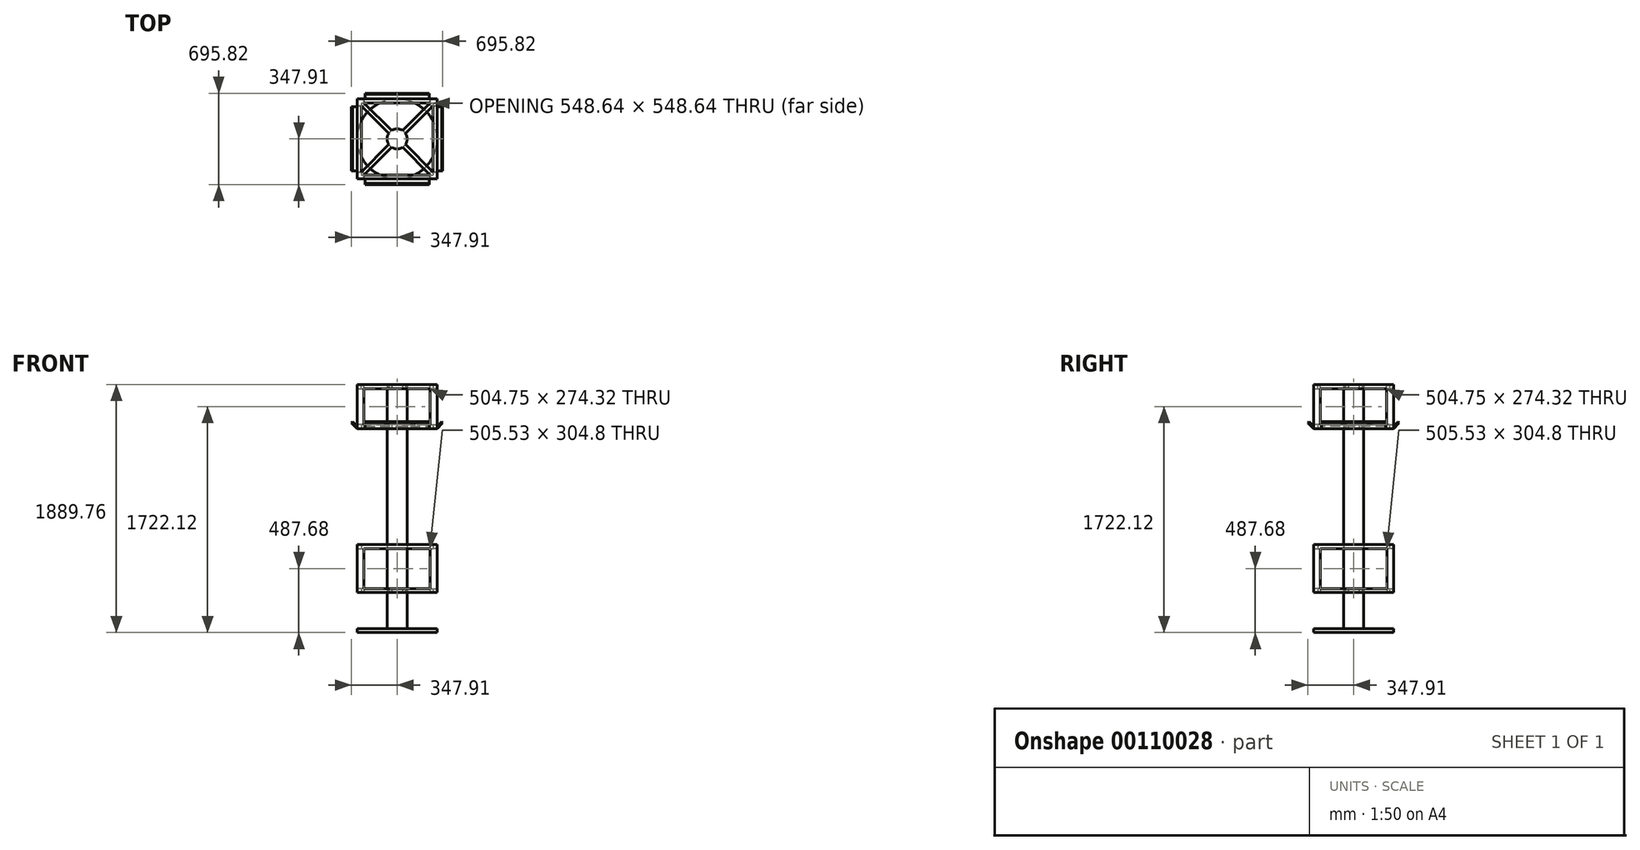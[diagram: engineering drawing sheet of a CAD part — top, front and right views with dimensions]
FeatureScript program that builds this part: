
annotation { "Feature Type Name" : "Feature", "Feature Type Description" : "" }
export const myFeature = defineFeature(function(context is Context, id is Id, definition is map)
    precondition{}
    {
        {
            var Q0;
            Q0=qCreatedBy(makeId("Top.planeOp"),FACE);
            var sketch = newSketch(context, id + "F0", { "sketchPlane" : qUnion([Q0])});
            skCircle(sketch, "E0", {"center": v(0, 0) * mm, "radius": 304.8 * mm});
            skSolve(sketch);
        }
        {
            var Q0;
            Q0 = qSketchRegion(id + "F0", true);
            extrude(context, id + "F1", {"entities" : qUnion([Q0]), "depth" : 30.48 * mm});
        }
        {
            var Q0;
            Q0=makeQuery(id+"F1.opExtrude","CAP_FACE",FACE,{"disambiguationData":[OSD([sQuery(id+"F0.wireOp",EDGE,"E0")])],"isStart":false});
            var sketch = newSketch(context, id + "F2", { "sketchPlane" : qUnion([Q0])});
            skCircle(sketch, "E1", {"center": v(0, 0) * mm, "radius": 76.2 * mm});
            skSolve(sketch);
        }
        {
            var Q0;
            Q0 = qSketchRegion(id + "F2", true);
            extrude(context, id + "F3", {"entities" : qUnion([Q0]), "operationType" : NewBodyOperationType.ADD, "depth" : 274.32 * mm});
        }
        {
            var Q0;
            Q0=makeQuery(id+"F3.opExtrude","CAP_FACE",FACE,{"disambiguationData":[OSD([sQuery(id+"F2.wireOp",EDGE,"E1")])],"isStart":false});
            var sketch = newSketch(context, id + "F4", { "sketchPlane" : qUnion([Q0])});
            skLineSegment(sketch, "E2.bottom", {"start": v(304.8, -304.8) * mm, "end": v(-304.8, -304.8) * mm});
            skLineSegment(sketch, "E2.top", {"start": v(304.8, 304.8) * mm, "end": v(-304.8, 304.8) * mm});
            skLineSegment(sketch, "E2.left", {"start": v(304.8, -304.8) * mm, "end": v(304.8, 304.8) * mm});
            skLineSegment(sketch, "E2.right", {"start": v(-304.8, -304.8) * mm, "end": v(-304.8, 304.8) * mm});
            skPoint(sketch, "E2.middle", {"position": v(0, 0) * mm});
            skLineSegment(sketch, "E3.bottom", {"start": v(252.77, -274.32) * mm, "end": v(-252.77, -274.32) * mm});
            skLineSegment(sketch, "E3.top", {"start": v(252.77, 274.32) * mm, "end": v(-252.77, 274.32) * mm});
            skLineSegment(sketch, "E3.left", {"start": v(274.32, -252.77) * mm, "end": v(274.32, 252.77) * mm});
            skLineSegment(sketch, "E3.right", {"start": v(-274.32, -252.77) * mm, "end": v(-274.32, 252.77) * mm});
            skLineSegment(sketch, "E4", {"start": v(-274.32, 274.32) * mm, "end": v(0, 0) * mm, "construction": true});
            skLineSegment(sketch, "E5", {"start": v(0, 0) * mm, "end": v(274.32, -274.32) * mm, "construction": true});
            skLineSegment(sketch, "E6", {"start": v(0, 0) * mm, "end": v(274.32, 274.32) * mm, "construction": true});
            skLineSegment(sketch, "E7", {"start": v(0, 0) * mm, "end": v(-274.32, -274.32) * mm, "construction": true});
            skLineSegment(sketch, "E8", {"start": v(0, 0) * mm, "end": v(-10.78, 10.78) * mm, "construction": true});
            skLineSegment(sketch, "E9", {"start": v(-10.78, 10.78) * mm, "end": v(0, 0) * mm, "construction": true});
            skLineSegment(sketch, "E10", {"start": v(0, 0) * mm, "end": v(10.78, 10.78) * mm, "construction": true});
            skLineSegment(sketch, "E11", {"start": v(10.78, 10.78) * mm, "end": v(0, 0) * mm, "construction": true});
            skLineSegment(sketch, "E12", {"start": v(0, 0) * mm, "end": v(53.88, -53.88) * mm, "construction": true});
            skLineSegment(sketch, "E13", {"start": v(0, 0) * mm, "end": v(-10.78, -10.78) * mm, "construction": true});
            skLineSegment(sketch, "E14", {"start": v(-10.78, -10.78) * mm, "end": v(0, 0) * mm, "construction": true});
            skLineSegment(sketch, "E15", {"start": v(0, 0) * mm, "end": v(10.78, -10.78) * mm, "construction": true});
            skLineSegment(sketch, "E16", {"start": v(10.78, -10.78) * mm, "end": v(0, 0) * mm, "construction": true});
            skLineSegment(sketch, "E17", {"start": v(-21.55, 0) * mm, "end": v(-274.32, -252.77) * mm});
            skLineSegment(sketch, "E18", {"start": v(0, -21.55) * mm, "end": v(-252.77, -274.32) * mm});
            skLineSegment(sketch, "E19", {"start": v(21.55, 0) * mm, "end": v(274.32, 252.77) * mm});
            skLineSegment(sketch, "E20", {"start": v(0, 21.55) * mm, "end": v(252.77, 274.32) * mm});
            skLineSegment(sketch, "E21", {"start": v(21.55, 0) * mm, "end": v(274.32, -252.77) * mm});
            skLineSegment(sketch, "E22", {"start": v(0, -21.55) * mm, "end": v(252.77, -274.32) * mm});
            skLineSegment(sketch, "E23", {"start": v(0, 21.55) * mm, "end": v(-252.77, 274.32) * mm});
            skLineSegment(sketch, "E24", {"start": v(-21.55, 0) * mm, "end": v(-274.32, 252.77) * mm});
            skSolve(sketch);
        }
        {
            var Q0;
            Q0 = qSketchRegion(id + "F4", true);
            extrude(context, id + "F5", {"entities" : qUnion([Q0]), "operationType" : NewBodyOperationType.ADD, "depth" : 30.48 * mm});
        }
        {
            var Q0;
            Q0=makeQuery(id+"F5.opExtrude","CAP_FACE",FACE,{"disambiguationData":[OSD([sQuery(id+"F4.wireOp",EDGE,"E2.bottom"),sQuery(id+"F4.wireOp",EDGE,"E2.top"),sQuery(id+"F4.wireOp",EDGE,"E2.left"),sQuery(id+"F4.wireOp",EDGE,"E2.right"),sQuery(id+"F4.wireOp",EDGE,"E3.bottom"),sQuery(id+"F4.wireOp",EDGE,"E3.top"),sQuery(id+"F4.wireOp",EDGE,"E3.left"),sQuery(id+"F4.wireOp",EDGE,"E3.right"),sQuery(id+"F4.wireOp",EDGE,"E17"),sQuery(id+"F4.wireOp",EDGE,"E18"),sQuery(id+"F4.wireOp",EDGE,"E19"),sQuery(id+"F4.wireOp",EDGE,"E20"),sQuery(id+"F4.wireOp",EDGE,"E21"),sQuery(id+"F4.wireOp",EDGE,"E22"),sQuery(id+"F4.wireOp",EDGE,"E23"),sQuery(id+"F4.wireOp",EDGE,"E24")])],"isStart":false});
            var sketch = newSketch(context, id + "F6", { "sketchPlane" : qUnion([Q0])});
            skCircle(sketch, "E25", {"center": v(0, 0) * mm, "radius": 76.2 * mm});
            skLineSegment(sketch, "E26.bottom", {"start": v(-304.8, 304.8) * mm, "end": v(-252.77, 304.8) * mm});
            skLineSegment(sketch, "E26.top", {"start": v(-304.8, 252.77) * mm, "end": v(-252.77, 252.77) * mm});
            skLineSegment(sketch, "E26.left", {"start": v(-304.8, 304.8) * mm, "end": v(-304.8, 252.77) * mm});
            skLineSegment(sketch, "E26.right", {"start": v(-252.77, 304.8) * mm, "end": v(-252.77, 252.77) * mm});
            skLineSegment(sketch, "E27.bottom", {"start": v(304.8, 304.8) * mm, "end": v(252.77, 304.8) * mm});
            skLineSegment(sketch, "E27.top", {"start": v(304.8, 252.77) * mm, "end": v(252.77, 252.77) * mm});
            skLineSegment(sketch, "E27.left", {"start": v(304.8, 304.8) * mm, "end": v(304.8, 252.77) * mm});
            skLineSegment(sketch, "E27.right", {"start": v(252.77, 304.8) * mm, "end": v(252.77, 252.77) * mm});
            skLineSegment(sketch, "E28.bottom", {"start": v(304.8, -304.8) * mm, "end": v(252.77, -304.8) * mm});
            skLineSegment(sketch, "E28.top", {"start": v(304.8, -252.77) * mm, "end": v(252.77, -252.77) * mm});
            skLineSegment(sketch, "E28.left", {"start": v(304.8, -304.8) * mm, "end": v(304.8, -252.77) * mm});
            skLineSegment(sketch, "E28.right", {"start": v(252.77, -304.8) * mm, "end": v(252.77, -252.77) * mm});
            skLineSegment(sketch, "E29.bottom", {"start": v(-304.8, -304.8) * mm, "end": v(-252.77, -304.8) * mm});
            skLineSegment(sketch, "E29.top", {"start": v(-304.8, -252.77) * mm, "end": v(-252.77, -252.77) * mm});
            skLineSegment(sketch, "E29.left", {"start": v(-304.8, -304.8) * mm, "end": v(-304.8, -252.77) * mm});
            skLineSegment(sketch, "E29.right", {"start": v(-252.77, -304.8) * mm, "end": v(-252.77, -252.77) * mm});
            skSolve(sketch);
        }
        {
            var Q0;
            Q0 = qSketchRegion(id + "F6", true);
            extrude(context, id + "F7", {"entities" : qUnion([Q0]), "operationType" : NewBodyOperationType.ADD, "depth" : 304.8 * mm, "hasSecondDirection" : true, "secondDirectionOppositeDirection" : true, "secondDirectionDepth" : 30.48 * mm});
        }
        {
            var Q0;
            Q0=makeQuery(id+"F7.opExtrude","CAP_FACE",FACE,{"disambiguationData":[OSD([sQuery(id+"F6.wireOp",EDGE,"E26.bottom"),sQuery(id+"F6.wireOp",EDGE,"E26.top"),sQuery(id+"F6.wireOp",EDGE,"E26.left"),sQuery(id+"F6.wireOp",EDGE,"E26.right")])],"isStart":false});
            var sketch = newSketch(context, id + "F8", { "sketchPlane" : qUnion([Q0])});
            skLineSegment(sketch, "E30.bottom", {"start": v(-304.8, 304.8) * mm, "end": v(304.8, 304.8) * mm});
            skLineSegment(sketch, "E30.top", {"start": v(-304.8, -304.8) * mm, "end": v(304.8, -304.8) * mm});
            skLineSegment(sketch, "E30.left", {"start": v(-304.8, 304.8) * mm, "end": v(-304.8, -304.8) * mm});
            skLineSegment(sketch, "E30.right", {"start": v(304.8, 304.8) * mm, "end": v(304.8, -304.8) * mm});
            skPoint(sketch, "E30.middle", {"position": v(0, 0) * mm});
            skLineSegment(sketch, "E31.bottom", {"start": v(-274.32, 274.32) * mm, "end": v(274.32, 274.32) * mm});
            skLineSegment(sketch, "E31.top", {"start": v(-274.32, -274.32) * mm, "end": v(274.32, -274.32) * mm});
            skLineSegment(sketch, "E31.left", {"start": v(-274.32, 274.32) * mm, "end": v(-274.32, -274.32) * mm});
            skLineSegment(sketch, "E31.right", {"start": v(274.32, 274.32) * mm, "end": v(274.32, -274.32) * mm});
            skSolve(sketch);
        }
        {
            var Q0;
            Q0 = qSketchRegion(id + "F8", true);
            var Q1;
            Q1=makeQuery(id+"F8.imprint","IMPRINT",FACE,{"disambiguationData":[TD([[makeQuery(id+"F8.imprint","IMPRINT",EDGE,{"derivedFrom":sQuery(id+"F8.wireOp",EDGE,"W6p5EcQz-eB1s-PhT1-Hnmv-3Ggb0HC7lHr9")}),1.0]])]});
            extrude(context, id + "F9", {"entities" : qUnion([Q0, Q1]), "operationType" : NewBodyOperationType.ADD, "depth" : 30.48 * mm});
        }
        {
            var Q0;
            Q0=makeQuery(id+"F7.opExtrude","CAP_FACE",FACE,{"disambiguationData":[OSD([sQuery(id+"F6.wireOp",EDGE,"E25")])],"isStart":false});
            var sketch = newSketch(context, id + "F10", { "sketchPlane" : qUnion([Q0])});
            skLineSegment(sketch, "E32.bottom", {"start": v(-304.8, 304.8) * mm, "end": v(304.8, 304.8) * mm});
            skLineSegment(sketch, "E32.top", {"start": v(-304.8, -304.8) * mm, "end": v(304.8, -304.8) * mm});
            skLineSegment(sketch, "E32.left", {"start": v(-304.8, 304.8) * mm, "end": v(-304.8, -304.8) * mm});
            skLineSegment(sketch, "E32.right", {"start": v(304.8, 304.8) * mm, "end": v(304.8, -304.8) * mm});
            skPoint(sketch, "E32.middle", {"position": v(0, 0) * mm});
            skLineSegment(sketch, "E33.bottom", {"start": v(-304.8, 304.8) * mm, "end": v(-252.37, 304.8) * mm});
            skLineSegment(sketch, "E33.top", {"start": v(-304.8, 252.37) * mm, "end": v(-252.37, 252.37) * mm});
            skLineSegment(sketch, "E33.left", {"start": v(-304.8, 304.8) * mm, "end": v(-304.8, 252.37) * mm});
            skLineSegment(sketch, "E33.right", {"start": v(-252.37, 304.8) * mm, "end": v(-252.37, 252.37) * mm});
            skLineSegment(sketch, "E34.bottom", {"start": v(-304.8, -304.8) * mm, "end": v(-252.37, -304.8) * mm});
            skLineSegment(sketch, "E34.top", {"start": v(-304.8, -252.37) * mm, "end": v(-252.37, -252.37) * mm});
            skLineSegment(sketch, "E34.left", {"start": v(-304.8, -304.8) * mm, "end": v(-304.8, -252.37) * mm});
            skLineSegment(sketch, "E34.right", {"start": v(-252.37, -304.8) * mm, "end": v(-252.37, -252.37) * mm});
            skLineSegment(sketch, "E35.bottom", {"start": v(304.8, 304.8) * mm, "end": v(252.37, 304.8) * mm});
            skLineSegment(sketch, "E35.top", {"start": v(304.8, 252.37) * mm, "end": v(252.37, 252.37) * mm});
            skLineSegment(sketch, "E35.left", {"start": v(304.8, 304.8) * mm, "end": v(304.8, 252.37) * mm});
            skLineSegment(sketch, "E35.right", {"start": v(252.37, 304.8) * mm, "end": v(252.37, 252.37) * mm});
            skLineSegment(sketch, "E36.bottom", {"start": v(304.8, -304.8) * mm, "end": v(252.37, -304.8) * mm});
            skLineSegment(sketch, "E36.top", {"start": v(304.8, -252.37) * mm, "end": v(252.37, -252.37) * mm});
            skLineSegment(sketch, "E36.left", {"start": v(304.8, -304.8) * mm, "end": v(304.8, -252.37) * mm});
            skLineSegment(sketch, "E36.right", {"start": v(252.37, -304.8) * mm, "end": v(252.37, -252.37) * mm});
            skCircle(sketch, "E37", {"center": v(0, 0) * mm, "radius": 76.2 * mm});
            skSolve(sketch);
        }
        {
            var Q0;
            Q0=makeQuery(id+"F10.imprint","IMPRINT",FACE,{"disambiguationData":[TD([[makeQuery(id+"F10.imprint","IMPRINT",EDGE,{"derivedFrom":sQuery(id+"F10.wireOp",EDGE,"E33.bottom")}),-1.0]])]});
            var Q1;
            Q1=makeQuery(id+"F10.imprint","IMPRINT",FACE,{"disambiguationData":[TD([[makeQuery(id+"F10.imprint","IMPRINT",EDGE,{"derivedFrom":sQuery(id+"F10.wireOp",EDGE,"E34.bottom")}),1.0]])]});
            var Q2;
            Q2=makeQuery(id+"F10.imprint","IMPRINT",FACE,{"disambiguationData":[TD([[makeQuery(id+"F10.imprint","IMPRINT",EDGE,{"derivedFrom":sQuery(id+"F10.wireOp",EDGE,"E35.bottom")}),1.0]])]});
            var Q3;
            Q3=makeQuery(id+"F10.imprint","IMPRINT",FACE,{"disambiguationData":[TD([[makeQuery(id+"F10.imprint","IMPRINT",EDGE,{"derivedFrom":sQuery(id+"F10.wireOp",EDGE,"E36.bottom")}),-1.0]])]});
            var Q4;
            Q4=makeQuery(id+"F10.imprint","IMPRINT",FACE,{"disambiguationData":[TD([[makeQuery(id+"F10.imprint","IMPRINT",EDGE,{"derivedFrom":sQuery(id+"F10.wireOp",EDGE,"E37")}),1.0]])]});
            extrude(context, id + "F11", {"entities" : qUnion([Q0, Q1, Q2, Q3, Q4]), "operationType" : NewBodyOperationType.ADD, "depth" : 914.4 * mm});
        }
        {
            var Q0;
            Q0=makeQuery(id+"F11.opExtrude","CAP_FACE",FACE,{"disambiguationData":[OSD([sQuery(id+"F10.wireOp",EDGE,"E37")])],"isStart":false});
            var sketch = newSketch(context, id + "F12", { "sketchPlane" : qUnion([Q0])});
            skLineSegment(sketch, "E38.bottom", {"start": v(304.8, -304.8) * mm, "end": v(-304.8, -304.8) * mm});
            skLineSegment(sketch, "E38.top", {"start": v(304.8, 304.8) * mm, "end": v(-304.8, 304.8) * mm});
            skLineSegment(sketch, "E38.left", {"start": v(304.8, -304.8) * mm, "end": v(304.8, 304.8) * mm});
            skLineSegment(sketch, "E38.right", {"start": v(-304.8, -304.8) * mm, "end": v(-304.8, 304.8) * mm});
            skPoint(sketch, "E38.middle", {"position": v(0, 0) * mm});
            skLineSegment(sketch, "E39.bottom", {"start": v(-252.37, 274.32) * mm, "end": v(252.37, 274.32) * mm});
            skLineSegment(sketch, "E39.top", {"start": v(-252.37, -274.32) * mm, "end": v(252.37, -274.32) * mm});
            skLineSegment(sketch, "E39.left", {"start": v(-274.32, 252.37) * mm, "end": v(-274.32, -252.37) * mm});
            skLineSegment(sketch, "E39.right", {"start": v(274.32, 252.37) * mm, "end": v(274.32, -252.37) * mm});
            skLineSegment(sketch, "E40.bottom", {"start": v(-304.8, 304.8) * mm, "end": v(-252.37, 304.8) * mm});
            skLineSegment(sketch, "E40.left", {"start": v(-304.8, 304.8) * mm, "end": v(-304.8, 252.37) * mm});
            skLineSegment(sketch, "E41.bottom", {"start": v(304.8, 304.8) * mm, "end": v(252.37, 304.8) * mm});
            skLineSegment(sketch, "E41.left", {"start": v(304.8, 304.8) * mm, "end": v(304.8, 252.37) * mm});
            skLineSegment(sketch, "E42.bottom", {"start": v(304.8, -304.8) * mm, "end": v(252.37, -304.8) * mm});
            skLineSegment(sketch, "E42.left", {"start": v(304.8, -304.8) * mm, "end": v(304.8, -252.37) * mm});
            skLineSegment(sketch, "E43.bottom", {"start": v(-304.8, -304.8) * mm, "end": v(-252.37, -304.8) * mm});
            skLineSegment(sketch, "E43.left", {"start": v(-304.8, -304.8) * mm, "end": v(-304.8, -252.37) * mm});
            skLineSegment(sketch, "E44", {"start": v(-274.32, 252.37) * mm, "end": v(-21.95, 0) * mm});
            skPoint(sketch, "E44.startSnap0", {"position": v(-278.59, 252.37) * mm});
            skLineSegment(sketch, "E45", {"start": v(-252.37, 274.32) * mm, "end": v(0, 21.95) * mm});
            skLineSegment(sketch, "E46", {"start": v(274.32, 252.37) * mm, "end": v(21.95, 0) * mm});
            skLineSegment(sketch, "E47", {"start": v(-274.32, -252.37) * mm, "end": v(-21.95, 0) * mm});
            skPoint(sketch, "E48.orphan", {"position": v(274.32, 274.32) * mm});
            skPoint(sketch, "E49.orphan", {"position": v(252.37, 252.37) * mm});
            skLineSegment(sketch, "E50.trimOffspring", {"start": v(21.95, 0) * mm, "end": v(274.32, -252.37) * mm});
            skLineSegment(sketch, "E51.trimOffspring", {"start": v(0, 21.95) * mm, "end": v(252.37, 274.32) * mm});
            skLineSegment(sketch, "E52.trimOffspring", {"start": v(0, -21.95) * mm, "end": v(252.37, -274.32) * mm});
            skLineSegment(sketch, "E53.trimOffspring", {"start": v(0, -21.95) * mm, "end": v(-252.37, -274.32) * mm});
            skPoint(sketch, "E54.orphan", {"position": v(-252.37, 252.37) * mm});
            skPoint(sketch, "E55.orphan", {"position": v(-274.32, 274.32) * mm});
            skPoint(sketch, "E56.orphan", {"position": v(-252.37, -252.37) * mm});
            skPoint(sketch, "E57.orphan", {"position": v(-274.32, -274.32) * mm});
            skPoint(sketch, "E58.orphan", {"position": v(274.32, -274.32) * mm});
            skPoint(sketch, "E42.right.end.orphan", {"position": v(252.37, -252.37) * mm});
            skSolve(sketch);
        }
        {
            var Q0;
            Q0 = qSketchRegion(id + "F12", true);
            extrude(context, id + "F13", {"entities" : qUnion([Q0]), "operationType" : NewBodyOperationType.ADD, "depth" : 30.48 * mm});
        }
        {
            var Q0;
            Q0=makeQuery(id+"F13.opExtrude","CAP_FACE",FACE,{"disambiguationData":[OSD([sQuery(id+"F12.wireOp",EDGE,"E38.bottom"),sQuery(id+"F12.wireOp",EDGE,"E38.top"),sQuery(id+"F12.wireOp",EDGE,"E38.left"),sQuery(id+"F12.wireOp",EDGE,"E38.right"),sQuery(id+"F12.wireOp",EDGE,"E39.bottom"),sQuery(id+"F12.wireOp",EDGE,"E39.top"),sQuery(id+"F12.wireOp",EDGE,"E39.left"),sQuery(id+"F12.wireOp",EDGE,"E39.right"),sQuery(id+"F12.wireOp",EDGE,"E40.bottom"),sQuery(id+"F12.wireOp",EDGE,"E40.left"),sQuery(id+"F12.wireOp",EDGE,"E41.bottom"),sQuery(id+"F12.wireOp",EDGE,"E41.left"),sQuery(id+"F12.wireOp",EDGE,"E42.bottom"),sQuery(id+"F12.wireOp",EDGE,"E42.left"),sQuery(id+"F12.wireOp",EDGE,"E43.bottom"),sQuery(id+"F12.wireOp",EDGE,"E43.left"),sQuery(id+"F12.wireOp",EDGE,"E44"),sQuery(id+"F12.wireOp",EDGE,"E45"),sQuery(id+"F12.wireOp",EDGE,"E46"),sQuery(id+"F12.wireOp",EDGE,"E47"),sQuery(id+"F12.wireOp",EDGE,"E50.trimOffspring"),sQuery(id+"F12.wireOp",EDGE,"E51.trimOffspring"),sQuery(id+"F12.wireOp",EDGE,"E52.trimOffspring"),sQuery(id+"F12.wireOp",EDGE,"E53.trimOffspring")])],"isStart":false});
            var sketch = newSketch(context, id + "F14", { "sketchPlane" : qUnion([Q0])});
            skLineSegment(sketch, "E59.bottom", {"start": v(-304.8, 304.8) * mm, "end": v(-252.37, 304.8) * mm});
            skLineSegment(sketch, "E59.top", {"start": v(-304.8, 252.37) * mm, "end": v(-252.37, 252.37) * mm});
            skLineSegment(sketch, "E59.left", {"start": v(-304.8, 304.8) * mm, "end": v(-304.8, 252.37) * mm});
            skLineSegment(sketch, "E59.right", {"start": v(-252.37, 304.8) * mm, "end": v(-252.37, 252.37) * mm});
            skLineSegment(sketch, "E60.bottom", {"start": v(304.8, 304.8) * mm, "end": v(252.37, 304.8) * mm});
            skLineSegment(sketch, "E60.top", {"start": v(304.8, 252.37) * mm, "end": v(252.37, 252.37) * mm});
            skLineSegment(sketch, "E60.left", {"start": v(304.8, 304.8) * mm, "end": v(304.8, 252.37) * mm});
            skLineSegment(sketch, "E60.right", {"start": v(252.37, 304.8) * mm, "end": v(252.37, 252.37) * mm});
            skLineSegment(sketch, "E61.bottom", {"start": v(304.8, -304.8) * mm, "end": v(252.37, -304.8) * mm});
            skLineSegment(sketch, "E61.top", {"start": v(304.8, -252.37) * mm, "end": v(252.37, -252.37) * mm});
            skLineSegment(sketch, "E61.left", {"start": v(304.8, -304.8) * mm, "end": v(304.8, -252.37) * mm});
            skLineSegment(sketch, "E61.right", {"start": v(252.37, -304.8) * mm, "end": v(252.37, -252.37) * mm});
            skLineSegment(sketch, "E62.bottom", {"start": v(-304.8, -304.8) * mm, "end": v(-252.37, -304.8) * mm});
            skLineSegment(sketch, "E62.top", {"start": v(-304.8, -252.37) * mm, "end": v(-252.37, -252.37) * mm});
            skLineSegment(sketch, "E62.left", {"start": v(-304.8, -304.8) * mm, "end": v(-304.8, -252.37) * mm});
            skLineSegment(sketch, "E62.right", {"start": v(-252.37, -304.8) * mm, "end": v(-252.37, -252.37) * mm});
            skCircle(sketch, "E63", {"center": v(0, 0) * mm, "radius": 76.2 * mm});
            skSolve(sketch);
        }
        {
            var Q0;
            Q0 = qSketchRegion(id + "F14", true);
            extrude(context, id + "F15", {"entities" : qUnion([Q0]), "operationType" : NewBodyOperationType.ADD, "depth" : 304.8 * mm, "hasSecondDirection" : true, "secondDirectionOppositeDirection" : true, "secondDirectionDepth" : 30.48 * mm});
        }
        {
            var Q0;
            Q0=makeQuery(id+"F15.opExtrude","CAP_FACE",FACE,{"disambiguationData":[OSD([sQuery(id+"F14.wireOp",EDGE,"E63")])],"isStart":false});
            var sketch = newSketch(context, id + "F16", { "sketchPlane" : qUnion([Q0])});
            skLineSegment(sketch, "E64.bottom", {"start": v(-304.8, 304.8) * mm, "end": v(304.8, 304.8) * mm});
            skLineSegment(sketch, "E64.top", {"start": v(-304.8, -304.8) * mm, "end": v(304.8, -304.8) * mm});
            skLineSegment(sketch, "E64.left", {"start": v(-304.8, 304.8) * mm, "end": v(-304.8, -304.8) * mm});
            skLineSegment(sketch, "E64.right", {"start": v(304.8, 304.8) * mm, "end": v(304.8, -304.8) * mm});
            skPoint(sketch, "E64.middle", {"position": v(0, 0) * mm});
            skLineSegment(sketch, "E65.bottom", {"start": v(-274.32, 274.32) * mm, "end": v(274.32, 274.32) * mm});
            skLineSegment(sketch, "E65.top", {"start": v(-274.32, -274.32) * mm, "end": v(274.32, -274.32) * mm});
            skLineSegment(sketch, "E65.left", {"start": v(-274.32, 274.32) * mm, "end": v(-274.32, -274.32) * mm});
            skLineSegment(sketch, "E65.right", {"start": v(274.32, 274.32) * mm, "end": v(274.32, -274.32) * mm});
            skSolve(sketch);
        }
        {
            var Q0;
            Q0 = qSketchRegion(id + "F16", true);
            extrude(context, id + "F17", {"entities" : qUnion([Q0]), "operationType" : NewBodyOperationType.ADD, "oppositeDirection" : true, "depth" : 30.48 * mm});
        }
        {
            var Q0;
            Q0=makeQuery(id+"F17.boolean.opBoolean","MERGE",FACE,{"derivedFrom":[makeQuery(id+"F15.opExtrude","CAP_FACE",FACE,{"disambiguationData":[OSD([sQuery(id+"F14.wireOp",EDGE,"E59.bottom"),sQuery(id+"F14.wireOp",EDGE,"E59.top"),sQuery(id+"F14.wireOp",EDGE,"E59.left"),sQuery(id+"F14.wireOp",EDGE,"E59.right")])],"isStart":false}),makeQuery(id+"F15.opExtrude","CAP_FACE",FACE,{"disambiguationData":[OSD([sQuery(id+"F14.wireOp",EDGE,"E60.bottom"),sQuery(id+"F14.wireOp",EDGE,"E60.top"),sQuery(id+"F14.wireOp",EDGE,"E60.left"),sQuery(id+"F14.wireOp",EDGE,"E60.right")])],"isStart":false}),makeQuery(id+"F15.opExtrude","CAP_FACE",FACE,{"disambiguationData":[OSD([sQuery(id+"F14.wireOp",EDGE,"E61.bottom"),sQuery(id+"F14.wireOp",EDGE,"E61.top"),sQuery(id+"F14.wireOp",EDGE,"E61.left"),sQuery(id+"F14.wireOp",EDGE,"E61.right")])],"isStart":false}),makeQuery(id+"F15.opExtrude","CAP_FACE",FACE,{"disambiguationData":[OSD([sQuery(id+"F14.wireOp",EDGE,"E62.bottom"),sQuery(id+"F14.wireOp",EDGE,"E62.top"),sQuery(id+"F14.wireOp",EDGE,"E62.left"),sQuery(id+"F14.wireOp",EDGE,"E62.right")])],"isStart":false}),makeQuery(id+"F17.opExtrude","CAP_FACE",FACE,{"disambiguationData":[OSD([sQuery(id+"F16.wireOp",EDGE,"E64.bottom"),sQuery(id+"F16.wireOp",EDGE,"E64.top"),sQuery(id+"F16.wireOp",EDGE,"E64.left"),sQuery(id+"F16.wireOp",EDGE,"E64.right"),sQuery(id+"F16.wireOp",EDGE,"E65.bottom"),sQuery(id+"F16.wireOp",EDGE,"E65.top"),sQuery(id+"F16.wireOp",EDGE,"E65.left"),sQuery(id+"F16.wireOp",EDGE,"E65.right")])],"isStart":true})]});
            var sketch = newSketch(context, id + "F18", { "sketchPlane" : qUnion([Q0])});
            skLineSegment(sketch, "E66.top", {"start": v(-252.37, 274.32) * mm, "end": v(-274.32, 274.32) * mm});
            skLineSegment(sketch, "E66.right", {"start": v(-274.32, 252.37) * mm, "end": v(-274.32, 274.32) * mm});
            skLineSegment(sketch, "E67.top", {"start": v(252.37, 274.32) * mm, "end": v(274.32, 274.32) * mm});
            skLineSegment(sketch, "E67.right", {"start": v(274.32, 252.37) * mm, "end": v(274.32, 274.32) * mm});
            skLineSegment(sketch, "E68.top", {"start": v(252.37, -274.32) * mm, "end": v(274.32, -274.32) * mm});
            skLineSegment(sketch, "E68.right", {"start": v(274.32, -252.37) * mm, "end": v(274.32, -274.32) * mm});
            skLineSegment(sketch, "E69.top", {"start": v(-252.37, -274.32) * mm, "end": v(-274.32, -274.32) * mm});
            skLineSegment(sketch, "E69.right", {"start": v(-274.32, -252.37) * mm, "end": v(-274.32, -274.32) * mm});
            skLineSegment(sketch, "E70", {"start": v(-274.32, 252.37) * mm, "end": v(-21.95, 0) * mm});
            skLineSegment(sketch, "E71", {"start": v(-252.37, 274.32) * mm, "end": v(0, 21.95) * mm});
            skLineSegment(sketch, "E72", {"start": v(274.32, 252.37) * mm, "end": v(21.95, 0) * mm});
            skLineSegment(sketch, "E73", {"start": v(-274.32, -252.37) * mm, "end": v(-21.95, 0) * mm});
            skLineSegment(sketch, "E74.trimOffspring", {"start": v(21.95, 0) * mm, "end": v(274.32, -252.37) * mm});
            skLineSegment(sketch, "E75.trimOffspring", {"start": v(0, 21.95) * mm, "end": v(252.37, 274.32) * mm});
            skLineSegment(sketch, "E76.trimOffspring", {"start": v(0, -21.95) * mm, "end": v(252.37, -274.32) * mm});
            skLineSegment(sketch, "E77.trimOffspring", {"start": v(0, -21.95) * mm, "end": v(-252.37, -274.32) * mm});
            skSolve(sketch);
        }
        {
            var Q0;
            Q0=makeQuery(id+"F17.boolean.opBoolean","MERGE",FACE,{"derivedFrom":[makeQuery(id+"F15.boolean.opBoolean","MERGE",FACE,{"derivedFrom":[makeQuery(id+"F13.boolean.opBoolean","MERGE",FACE,{"derivedFrom":[makeQuery(id+"F11.boolean.opBoolean","MERGE",FACE,{"derivedFrom":[makeQuery(id+"F9.boolean.opBoolean","MERGE",FACE,{"derivedFrom":[makeQuery(id+"F7.boolean.opBoolean","MERGE",FACE,{"derivedFrom":[makeQuery(id+"F5.opExtrude","SWEPT_FACE",FACE,{"disambiguationData":[OSD([sQuery(id+"F4.wireOp",EDGE,"E2.bottom")])]}),makeQuery(id+"F7.opExtrude","SWEPT_FACE",FACE,{"disambiguationData":[OSD([sQuery(id+"F6.wireOp",EDGE,"E28.bottom")])]}),makeQuery(id+"F7.opExtrude","SWEPT_FACE",FACE,{"disambiguationData":[OSD([sQuery(id+"F6.wireOp",EDGE,"E29.bottom")])]})]}),makeQuery(id+"F9.opExtrude","SWEPT_FACE",FACE,{"disambiguationData":[OSD([sQuery(id+"F8.wireOp",EDGE,"E30.top")])]})]}),makeQuery(id+"F11.opExtrude","SWEPT_FACE",FACE,{"disambiguationData":[OSD([sQuery(id+"F10.wireOp",EDGE,"E34.bottom")])]}),makeQuery(id+"F11.opExtrude","SWEPT_FACE",FACE,{"disambiguationData":[OSD([sQuery(id+"F10.wireOp",EDGE,"E36.bottom")])]})]}),makeQuery(id+"F13.opExtrude","SWEPT_FACE",FACE,{"disambiguationData":[OSD([sQuery(id+"F12.wireOp",EDGE,"E38.bottom"),sQuery(id+"F12.wireOp",EDGE,"E42.bottom"),sQuery(id+"F12.wireOp",EDGE,"E43.bottom")])]})]}),makeQuery(id+"F15.opExtrude","SWEPT_FACE",FACE,{"disambiguationData":[OSD([sQuery(id+"F14.wireOp",EDGE,"E61.bottom")])]}),makeQuery(id+"F15.opExtrude","SWEPT_FACE",FACE,{"disambiguationData":[OSD([sQuery(id+"F14.wireOp",EDGE,"E62.bottom")])]})]}),makeQuery(id+"F17.opExtrude","SWEPT_FACE",FACE,{"disambiguationData":[OSD([sQuery(id+"F16.wireOp",EDGE,"E64.top")])]})]});
            var sketch = newSketch(context, id + "F19", { "sketchPlane" : qUnion([Q0])});
            skLineSegment(sketch, "E78", {"start": v(-252.37, 1554.48) * mm, "end": v(-304.8, 1554.48) * mm, "construction": true});
            skLineSegment(sketch, "E79", {"start": v(-304.8, 1554.48) * mm, "end": v(-347.9, 1597.59) * mm, "construction": true});
            skLineSegment(sketch, "E80", {"start": v(-347.9, 1597.59) * mm, "end": v(-339.28, 1606.2) * mm, "construction": true});
            skLineSegment(sketch, "E81", {"start": v(-304.8, 1554.48) * mm, "end": v(-347.9, 1597.59) * mm});
            skLineSegment(sketch, "E82", {"start": v(-347.9, 1597.59) * mm, "end": v(-339.28, 1606.2) * mm});
            skLineSegment(sketch, "E83", {"start": v(-339.28, 1606.2) * mm, "end": v(-304.8, 1571.72) * mm});
            skLineSegment(sketch, "E84", {"start": v(-304.8, 1571.72) * mm, "end": v(-274.32, 1571.72) * mm});
            skLineSegment(sketch, "E85", {"start": v(-274.32, 1571.72) * mm, "end": v(-274.32, 1554.48) * mm});
            skLineSegment(sketch, "E86", {"start": v(-274.32, 1554.48) * mm, "end": v(-304.8, 1554.48) * mm});
            skLineSegment(sketch, "E87", {"start": v(252.37, 1554.48) * mm, "end": v(304.8, 1554.48) * mm, "construction": true});
            skLineSegment(sketch, "E88", {"start": v(304.8, 1554.48) * mm, "end": v(347.9, 1597.59) * mm, "construction": true});
            skLineSegment(sketch, "E89", {"start": v(347.9, 1597.59) * mm, "end": v(339.28, 1606.2) * mm, "construction": true});
            skLineSegment(sketch, "E90", {"start": v(304.8, 1554.48) * mm, "end": v(274.32, 1554.48) * mm});
            skLineSegment(sketch, "E91", {"start": v(304.8, 1554.48) * mm, "end": v(347.9, 1597.59) * mm});
            skLineSegment(sketch, "E92", {"start": v(347.9, 1597.59) * mm, "end": v(339.28, 1606.2) * mm});
            skLineSegment(sketch, "E93", {"start": v(339.28, 1606.2) * mm, "end": v(304.8, 1571.72) * mm});
            skLineSegment(sketch, "E94", {"start": v(304.8, 1571.72) * mm, "end": v(274.32, 1571.72) * mm});
            skLineSegment(sketch, "E95", {"start": v(274.32, 1554.48) * mm, "end": v(274.32, 1571.72) * mm});
            skSolve(sketch);
        }
        {
            var Q0;
            Q0 = qSketchRegion(id + "F19", true);
            extrude(context, id + "F20", {"entities" : qUnion([Q0]), "operationType" : NewBodyOperationType.ADD, "oppositeDirection" : true, "depth" : 609.6 * mm});
        }
        {
            var Q0;
            {var subQ2=sQuery(id+"F10.wireOp",EDGE,"E36.left");var subQ4=sQuery(id+"F10.wireOp",EDGE,"E35.left");var subQ15=sQuery(id+"F8.wireOp",EDGE,"E30.right");var subQ30=sQuery(id+"F4.wireOp",EDGE,"E2.left");var subQ39=sQuery(id+"F12.wireOp",EDGE,"E42.left");var subQ41=sQuery(id+"F12.wireOp",EDGE,"E41.left");var subQ44=sQuery(id+"F12.wireOp",EDGE,"E38.left");Q0=makeQuery(id+"F20.boolean.opBoolean","SPLIT",FACE,{"disambiguationData":[TD([makeQuery(id+"F7.opExtrude","SWEPT_FACE",FACE,{"disambiguationData":[OSD([sQuery(id+"F6.wireOp",EDGE,"E27.top")])]})])],"derivedFrom":makeQuery(id+"F17.boolean.opBoolean","MERGE",FACE,{"derivedFrom":[makeQuery(id+"F15.boolean.opBoolean","MERGE",FACE,{"derivedFrom":[makeQuery(id+"F13.boolean.opBoolean","MERGE",FACE,{"derivedFrom":[makeQuery(id+"F11.boolean.opBoolean","MERGE",FACE,{"derivedFrom":[makeQuery(id+"F9.boolean.opBoolean","MERGE",FACE,{"derivedFrom":[makeQuery(id+"F7.boolean.opBoolean","MERGE",FACE,{"derivedFrom":[makeQuery(id+"F5.opExtrude","SWEPT_FACE",FACE,{"disambiguationData":[OSD([subQ30])]}),makeQuery(id+"F7.opExtrude","SWEPT_FACE",FACE,{"disambiguationData":[OSD([sQuery(id+"F6.wireOp",EDGE,"E27.left")])]}),makeQuery(id+"F7.opExtrude","SWEPT_FACE",FACE,{"disambiguationData":[OSD([sQuery(id+"F6.wireOp",EDGE,"E28.left")])]})]}),makeQuery(id+"F9.opExtrude","SWEPT_FACE",FACE,{"disambiguationData":[OSD([subQ15])]})]}),makeQuery(id+"F11.opExtrude","SWEPT_FACE",FACE,{"disambiguationData":[OSD([subQ4])]}),makeQuery(id+"F11.opExtrude","SWEPT_FACE",FACE,{"disambiguationData":[OSD([subQ2])]})]}),makeQuery(id+"F13.opExtrude","SWEPT_FACE",FACE,{"disambiguationData":[OSD([subQ44,subQ41,subQ39])]})]}),makeQuery(id+"F15.opExtrude","SWEPT_FACE",FACE,{"disambiguationData":[OSD([sQuery(id+"F14.wireOp",EDGE,"E60.left")])]}),makeQuery(id+"F15.opExtrude","SWEPT_FACE",FACE,{"disambiguationData":[OSD([sQuery(id+"F14.wireOp",EDGE,"E61.left")])]})]}),makeQuery(id+"F17.opExtrude","SWEPT_FACE",FACE,{"disambiguationData":[OSD([sQuery(id+"F16.wireOp",EDGE,"E64.right")])]})]})});}
            var sketch = newSketch(context, id + "F21", { "sketchPlane" : qUnion([Q0])});
            skLineSegment(sketch, "E96", {"start": v(274.32, 1554.48) * mm, "end": v(304.8, 1554.48) * mm});
            skLineSegment(sketch, "E97", {"start": v(304.8, 1554.48) * mm, "end": v(347.9, 1597.59) * mm});
            skLineSegment(sketch, "E98", {"start": v(347.9, 1597.59) * mm, "end": v(339.28, 1606.2) * mm});
            skLineSegment(sketch, "E99", {"start": v(339.28, 1606.2) * mm, "end": v(304.8, 1571.72) * mm});
            skLineSegment(sketch, "E100", {"start": v(304.8, 1571.72) * mm, "end": v(274.32, 1571.72) * mm});
            skLineSegment(sketch, "E101", {"start": v(274.32, 1571.72) * mm, "end": v(274.32, 1554.48) * mm});
            skLineSegment(sketch, "E102", {"start": v(-274.32, 1554.48) * mm, "end": v(-304.8, 1554.48) * mm});
            skLineSegment(sketch, "E103", {"start": v(-304.8, 1554.48) * mm, "end": v(-347.9, 1597.59) * mm});
            skLineSegment(sketch, "E104", {"start": v(-347.9, 1597.59) * mm, "end": v(-339.28, 1606.2) * mm});
            skLineSegment(sketch, "E105", {"start": v(-339.28, 1606.2) * mm, "end": v(-304.8, 1571.72) * mm});
            skLineSegment(sketch, "E106", {"start": v(-304.8, 1571.72) * mm, "end": v(-274.32, 1571.72) * mm});
            skLineSegment(sketch, "E107", {"start": v(-274.32, 1571.72) * mm, "end": v(-274.32, 1554.48) * mm});
            skSolve(sketch);
        }
        {
            var Q0;
            Q0 = qSketchRegion(id + "F21", true);
            extrude(context, id + "F22", {"entities" : qUnion([Q0]), "operationType" : NewBodyOperationType.ADD, "oppositeDirection" : true, "depth" : 609.6 * mm});
        }
        {
            var Q0;
            Q0 = qSketchRegion(id + "F18", true);
            extrude(context, id + "F23", {"entities" : qUnion([Q0]), "operationType" : NewBodyOperationType.ADD, "oppositeDirection" : true, "depth" : 30.48 * mm});
        }
        {
            var Q0;
            Q0=makeQuery(id+"F23.boolean.opBoolean","MERGE",FACE,{"derivedFrom":[makeQuery(id+"F15.opExtrude","CAP_FACE",FACE,{"disambiguationData":[OSD([sQuery(id+"F14.wireOp",EDGE,"E63")])],"isStart":false}),makeQuery(id+"F17.boolean.opBoolean","MERGE",FACE,{"derivedFrom":[makeQuery(id+"F15.opExtrude","CAP_FACE",FACE,{"disambiguationData":[OSD([sQuery(id+"F14.wireOp",EDGE,"E59.bottom"),sQuery(id+"F14.wireOp",EDGE,"E59.top"),sQuery(id+"F14.wireOp",EDGE,"E59.left"),sQuery(id+"F14.wireOp",EDGE,"E59.right")])],"isStart":false}),makeQuery(id+"F15.opExtrude","CAP_FACE",FACE,{"disambiguationData":[OSD([sQuery(id+"F14.wireOp",EDGE,"E60.bottom"),sQuery(id+"F14.wireOp",EDGE,"E60.top"),sQuery(id+"F14.wireOp",EDGE,"E60.left"),sQuery(id+"F14.wireOp",EDGE,"E60.right")])],"isStart":false}),makeQuery(id+"F15.opExtrude","CAP_FACE",FACE,{"disambiguationData":[OSD([sQuery(id+"F14.wireOp",EDGE,"E61.bottom"),sQuery(id+"F14.wireOp",EDGE,"E61.top"),sQuery(id+"F14.wireOp",EDGE,"E61.left"),sQuery(id+"F14.wireOp",EDGE,"E61.right")])],"isStart":false}),makeQuery(id+"F15.opExtrude","CAP_FACE",FACE,{"disambiguationData":[OSD([sQuery(id+"F14.wireOp",EDGE,"E62.bottom"),sQuery(id+"F14.wireOp",EDGE,"E62.top"),sQuery(id+"F14.wireOp",EDGE,"E62.left"),sQuery(id+"F14.wireOp",EDGE,"E62.right")])],"isStart":false}),makeQuery(id+"F17.opExtrude","CAP_FACE",FACE,{"disambiguationData":[OSD([sQuery(id+"F16.wireOp",EDGE,"E64.bottom"),sQuery(id+"F16.wireOp",EDGE,"E64.top"),sQuery(id+"F16.wireOp",EDGE,"E64.left"),sQuery(id+"F16.wireOp",EDGE,"E64.right"),sQuery(id+"F16.wireOp",EDGE,"E65.bottom"),sQuery(id+"F16.wireOp",EDGE,"E65.top"),sQuery(id+"F16.wireOp",EDGE,"E65.left"),sQuery(id+"F16.wireOp",EDGE,"E65.right")])],"isStart":true})]}),makeQuery(id+"F23.opExtrude","CAP_FACE",FACE,{"disambiguationData":[OSD([sQuery(id+"F18.wireOp",EDGE,"E66.top"),sQuery(id+"F18.wireOp",EDGE,"E66.right"),sQuery(id+"F18.wireOp",EDGE,"E67.top"),sQuery(id+"F18.wireOp",EDGE,"E67.right"),sQuery(id+"F18.wireOp",EDGE,"E68.top"),sQuery(id+"F18.wireOp",EDGE,"E68.right"),sQuery(id+"F18.wireOp",EDGE,"E69.top"),sQuery(id+"F18.wireOp",EDGE,"E69.right"),sQuery(id+"F18.wireOp",EDGE,"E70"),sQuery(id+"F18.wireOp",EDGE,"E71"),sQuery(id+"F18.wireOp",EDGE,"E72"),sQuery(id+"F18.wireOp",EDGE,"E73"),sQuery(id+"F18.wireOp",EDGE,"E74.trimOffspring"),sQuery(id+"F18.wireOp",EDGE,"E75.trimOffspring"),sQuery(id+"F18.wireOp",EDGE,"E76.trimOffspring"),sQuery(id+"F18.wireOp",EDGE,"E77.trimOffspring")])],"isStart":true})]});
            var sketch = newSketch(context, id + "F24", { "sketchPlane" : qUnion([Q0])});
            skLineSegment(sketch, "E108.bottom", {"start": v(-304.8, 304.8) * mm, "end": v(-243.84, 304.8) * mm});
            skLineSegment(sketch, "E108.top", {"start": v(-304.8, 376.98) * mm, "end": v(-243.84, 376.98) * mm});
            skLineSegment(sketch, "E108.left", {"start": v(-304.8, 304.8) * mm, "end": v(-304.8, 376.98) * mm});
            skLineSegment(sketch, "E108.right", {"start": v(-243.84, 304.8) * mm, "end": v(-243.84, 376.98) * mm});
            skLineSegment(sketch, "E109.bottom", {"start": v(304.8, 304.8) * mm, "end": v(243.84, 304.8) * mm});
            skLineSegment(sketch, "E109.top", {"start": v(304.8, 379.71) * mm, "end": v(243.84, 379.71) * mm});
            skLineSegment(sketch, "E109.left", {"start": v(304.8, 304.8) * mm, "end": v(304.8, 379.71) * mm});
            skLineSegment(sketch, "E109.right", {"start": v(243.84, 304.8) * mm, "end": v(243.84, 379.71) * mm});
            skLineSegment(sketch, "E110.bottom", {"start": v(304.8, 304.8) * mm, "end": v(390.85, 304.8) * mm});
            skLineSegment(sketch, "E110.top", {"start": v(304.8, 243.84) * mm, "end": v(390.85, 243.84) * mm});
            skLineSegment(sketch, "E110.left", {"start": v(304.8, 304.8) * mm, "end": v(304.8, 243.84) * mm});
            skLineSegment(sketch, "E110.right", {"start": v(390.85, 304.8) * mm, "end": v(390.85, 243.84) * mm});
            skLineSegment(sketch, "E111.bottom", {"start": v(304.8, -304.8) * mm, "end": v(378.54, -304.8) * mm});
            skLineSegment(sketch, "E111.top", {"start": v(304.8, -243.84) * mm, "end": v(378.54, -243.84) * mm});
            skLineSegment(sketch, "E111.left", {"start": v(304.8, -304.8) * mm, "end": v(304.8, -243.84) * mm});
            skLineSegment(sketch, "E111.right", {"start": v(378.54, -304.8) * mm, "end": v(378.54, -243.84) * mm});
            skLineSegment(sketch, "E112.bottom", {"start": v(304.8, -304.8) * mm, "end": v(243.84, -304.8) * mm});
            skLineSegment(sketch, "E112.top", {"start": v(304.8, -378.3) * mm, "end": v(243.84, -378.3) * mm});
            skLineSegment(sketch, "E112.left", {"start": v(304.8, -304.8) * mm, "end": v(304.8, -378.3) * mm});
            skLineSegment(sketch, "E112.right", {"start": v(243.84, -304.8) * mm, "end": v(243.84, -378.3) * mm});
            skLineSegment(sketch, "E113.bottom", {"start": v(-304.8, -304.8) * mm, "end": v(-243.84, -304.8) * mm});
            skLineSegment(sketch, "E113.top", {"start": v(-304.8, -385.14) * mm, "end": v(-243.84, -385.14) * mm});
            skLineSegment(sketch, "E113.left", {"start": v(-304.8, -304.8) * mm, "end": v(-304.8, -385.14) * mm});
            skLineSegment(sketch, "E113.right", {"start": v(-243.84, -304.8) * mm, "end": v(-243.84, -385.14) * mm});
            skLineSegment(sketch, "E114.bottom", {"start": v(-304.8, -304.8) * mm, "end": v(-378.1, -304.8) * mm});
            skLineSegment(sketch, "E114.top", {"start": v(-304.8, -243.84) * mm, "end": v(-378.1, -243.84) * mm});
            skLineSegment(sketch, "E114.left", {"start": v(-304.8, -304.8) * mm, "end": v(-304.8, -243.84) * mm});
            skLineSegment(sketch, "E114.right", {"start": v(-378.1, -304.8) * mm, "end": v(-378.1, -243.84) * mm});
            skLineSegment(sketch, "E115.bottom", {"start": v(-304.8, 304.8) * mm, "end": v(-365.76, 304.8) * mm});
            skLineSegment(sketch, "E115.top", {"start": v(-304.8, 243.84) * mm, "end": v(-365.76, 243.84) * mm});
            skLineSegment(sketch, "E115.left", {"start": v(-304.8, 304.8) * mm, "end": v(-304.8, 243.84) * mm});
            skLineSegment(sketch, "E115.right", {"start": v(-365.76, 304.8) * mm, "end": v(-365.76, 243.84) * mm});
            skSolve(sketch);
        }
        {
            var Q0;
            Q0 = qSketchRegion(id + "F24", true);
            extrude(context, id + "F25", {"entities" : qUnion([Q0]), "operationType" : NewBodyOperationType.REMOVE, "oppositeDirection" : true, "depth" : 609.6 * mm});
        }
    });
